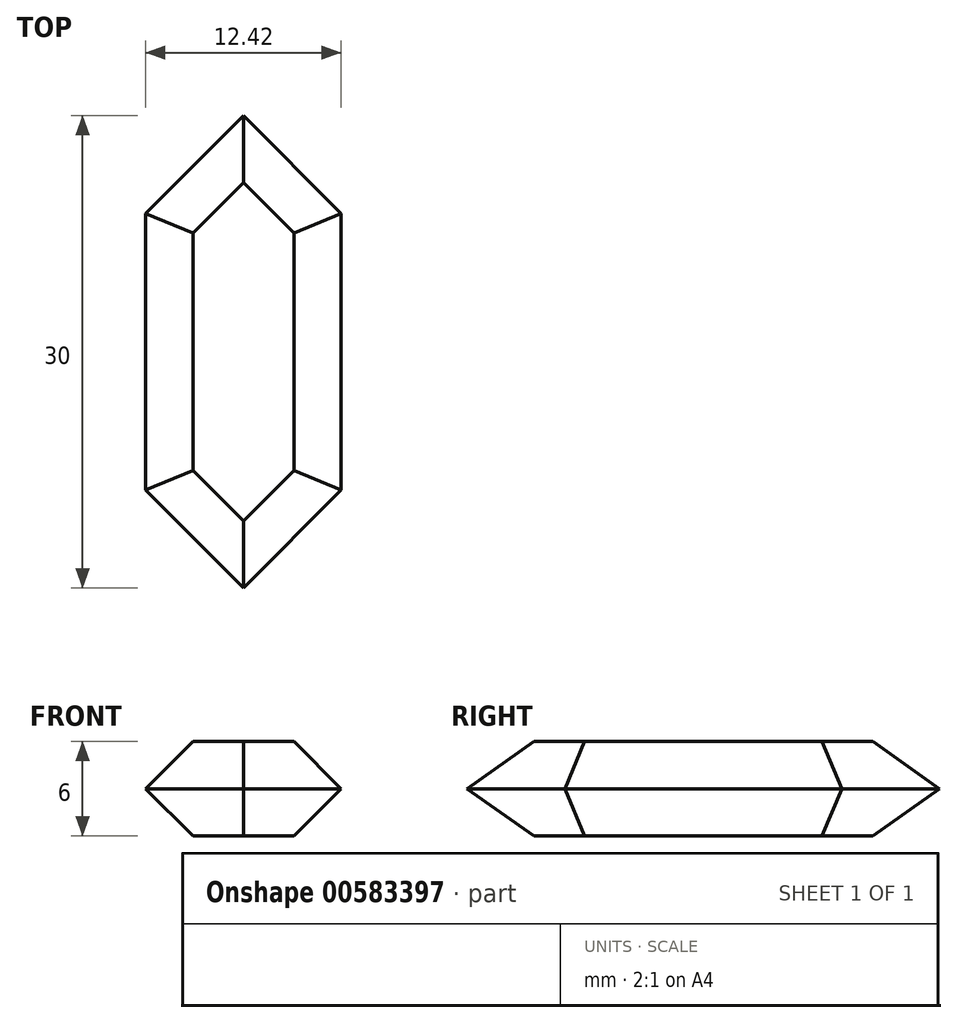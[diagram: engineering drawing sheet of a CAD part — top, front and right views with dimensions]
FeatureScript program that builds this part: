
annotation { "Feature Type Name" : "Feature", "Feature Type Description" : "" }
export const myFeature = defineFeature(function(context is Context, id is Id, definition is map)
    precondition{}
    {
        {
            var Q0;
            Q0=qCreatedBy(makeId("Top.planeOp"),FACE);
            var sketch = newSketch(context, id + "F0", { "sketchPlane" : qUnion([Q0])});
            skLineSegment(sketch, "E0", {"start": v(-6.21, 0) * mm, "end": v(-6.21, 8.79) * mm});
            skLineSegment(sketch, "E1", {"start": v(-6.21, 8.79) * mm, "end": v(0, 15) * mm});
            skLineSegment(sketch, "E2.MirrorCS", {"start": v(6.21, 8.79) * mm, "end": v(0, 15) * mm});
            skLineSegment(sketch, "E3.MirrorCS", {"start": v(6.21, 0) * mm, "end": v(6.21, 8.79) * mm});
            skLineSegment(sketch, "E4.MirrorCS", {"start": v(-6.21, 0) * mm, "end": v(-6.21, -8.79) * mm});
            skLineSegment(sketch, "E5.MirrorCS", {"start": v(-6.21, -8.79) * mm, "end": v(0, -15) * mm});
            skLineSegment(sketch, "E6.MirrorCS", {"start": v(6.21, -8.79) * mm, "end": v(0, -15) * mm});
            skLineSegment(sketch, "E7.MirrorCS", {"start": v(6.21, 0) * mm, "end": v(6.21, -8.79) * mm});
            skSolve(sketch);
        }
        {
            var Q0;
            Q0=qSketchRegion(id+"F0",true);
            extrude(context, id + "F1", {"entities" : qUnion([Q0]), "depth" : 6 * mm});
        }
        {
            var Q0;
            Q0=makeQuery(id+"F1.opExtrude","CAP_EDGE",EDGE,{"disambiguationData":[OSD([sQuery(id+"F0.wireOp",EDGE,"E1")])],"isStart":false});
            var Q1;
            Q1=makeQuery(id+"F1.opExtrude","CAP_EDGE",EDGE,{"disambiguationData":[OSD([sQuery(id+"F0.wireOp",EDGE,"E2.MirrorCS")])],"isStart":false});
            var Q2;
            Q2=makeQuery(id+"F1.opExtrude","CAP_EDGE",EDGE,{"disambiguationData":[OSD([sQuery(id+"F0.wireOp",EDGE,"E3.MirrorCS"),sQuery(id+"F0.wireOp",EDGE,"E7.MirrorCS")])],"isStart":false});
            var Q3;
            Q3=makeQuery(id+"F1.opExtrude","CAP_EDGE",EDGE,{"disambiguationData":[OSD([sQuery(id+"F0.wireOp",EDGE,"E0"),sQuery(id+"F0.wireOp",EDGE,"E4.MirrorCS")])],"isStart":false});
            var Q4;
            Q4=makeQuery(id+"F1.opExtrude","CAP_EDGE",EDGE,{"disambiguationData":[OSD([sQuery(id+"F0.wireOp",EDGE,"E5.MirrorCS")])],"isStart":false});
            var Q5;
            Q5=makeQuery(id+"F1.opExtrude","CAP_EDGE",EDGE,{"disambiguationData":[OSD([sQuery(id+"F0.wireOp",EDGE,"E6.MirrorCS")])],"isStart":false});
            var Q6;
            Q6=makeQuery(id+"F1.opExtrude","CAP_EDGE",EDGE,{"disambiguationData":[OSD([sQuery(id+"F0.wireOp",EDGE,"E1")])],"isStart":true});
            var Q7;
            Q7=makeQuery(id+"F1.opExtrude","CAP_EDGE",EDGE,{"disambiguationData":[OSD([sQuery(id+"F0.wireOp",EDGE,"E0"),sQuery(id+"F0.wireOp",EDGE,"E4.MirrorCS")])],"isStart":true});
            var Q8;
            Q8=makeQuery(id+"F1.opExtrude","CAP_EDGE",EDGE,{"disambiguationData":[OSD([sQuery(id+"F0.wireOp",EDGE,"E5.MirrorCS")])],"isStart":true});
            var Q9;
            Q9=makeQuery(id+"F1.opExtrude","CAP_EDGE",EDGE,{"disambiguationData":[OSD([sQuery(id+"F0.wireOp",EDGE,"E6.MirrorCS")])],"isStart":true});
            var Q10;
            Q10=makeQuery(id+"F1.opExtrude","CAP_EDGE",EDGE,{"disambiguationData":[OSD([sQuery(id+"F0.wireOp",EDGE,"E3.MirrorCS"),sQuery(id+"F0.wireOp",EDGE,"E7.MirrorCS")])],"isStart":true});
            var Q11;
            Q11=makeQuery(id+"F1.opExtrude","CAP_EDGE",EDGE,{"disambiguationData":[OSD([sQuery(id+"F0.wireOp",EDGE,"E2.MirrorCS")])],"isStart":true});
            chamfer(context, id + "F2", {"entities" : qUnion([Q0, Q1, Q2, Q3, Q4, Q5, Q6, Q7, Q8, Q9, Q10, Q11]), "width" : 3 * mm, "tangentPropagation" : true});
        }
    });
